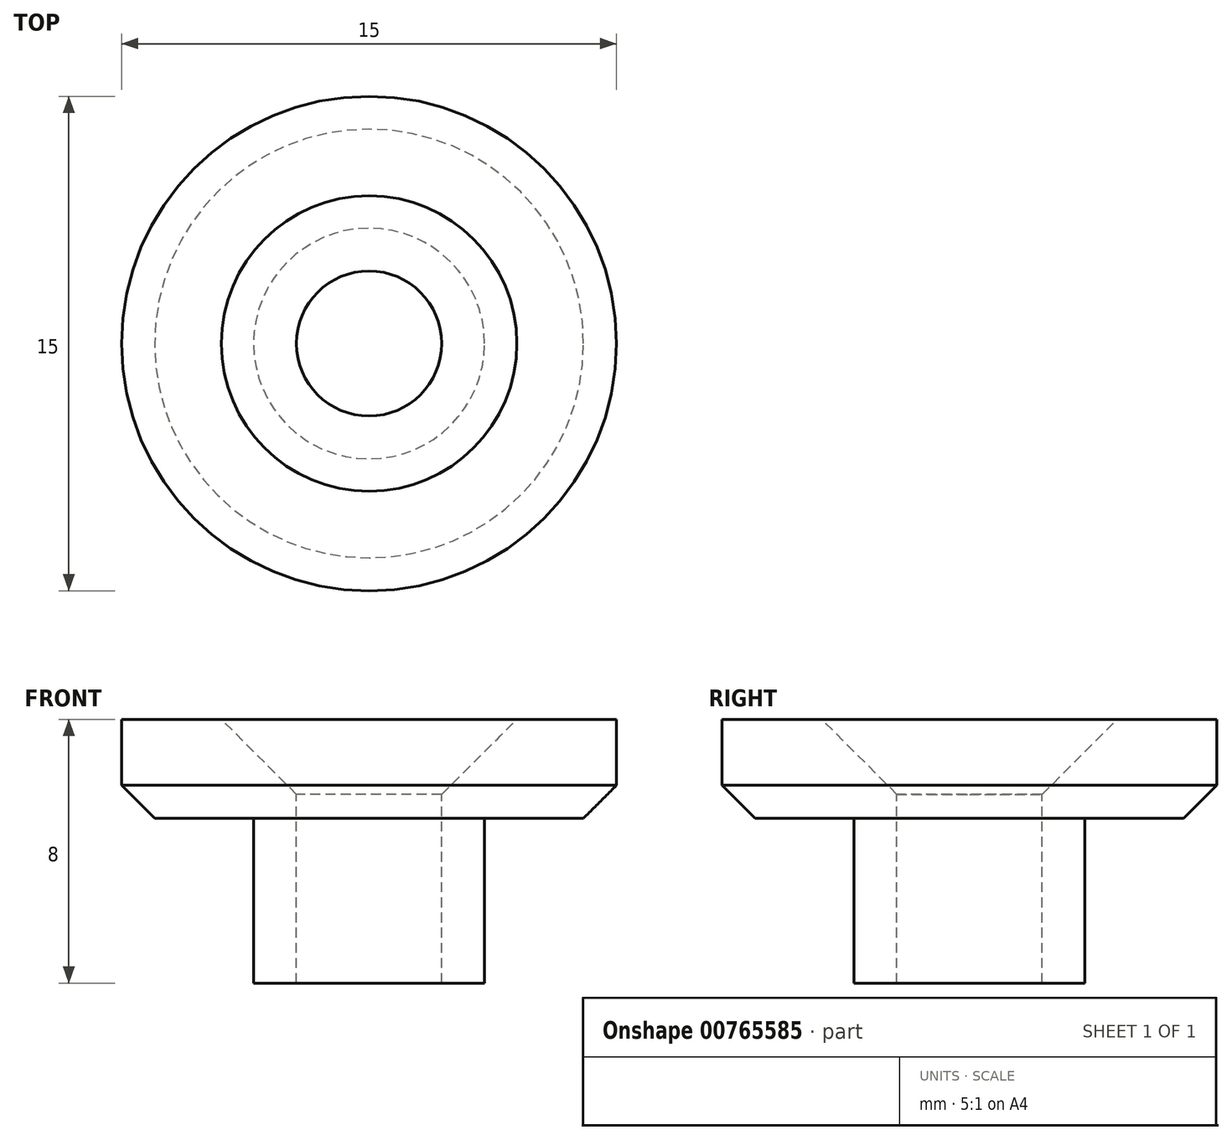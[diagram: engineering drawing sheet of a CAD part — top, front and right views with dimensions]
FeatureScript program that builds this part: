
annotation { "Feature Type Name" : "Feature", "Feature Type Description" : "" }
export const myFeature = defineFeature(function(context is Context, id is Id, definition is map)
    precondition{}
    {
        {
            var Q0;
            Q0=qCreatedBy(makeId("Front.planeOp"),FACE);
            var sketch = newSketch(context, id + "F0", { "sketchPlane" : qUnion([Q0])});
            skLineSegment(sketch, "E0", {"start": v(0, 0) * mm, "end": v(0, 8) * mm});
            skLineSegment(sketch, "E1", {"start": v(0, 8) * mm, "end": v(7.5, 8) * mm});
            skLineSegment(sketch, "E2", {"start": v(7.5, 8) * mm, "end": v(7.5, 5) * mm});
            skLineSegment(sketch, "E3", {"start": v(7.5, 5) * mm, "end": v(3.5, 5) * mm});
            skLineSegment(sketch, "E4", {"start": v(3.5, 5) * mm, "end": v(3.5, 0) * mm});
            skLineSegment(sketch, "E5", {"start": v(3.5, 0) * mm, "end": v(0, 0) * mm});
            skSolve(sketch);
        }
        {
            var Q0;
            Q0=makeQuery(id+"F0.imprint","IMPRINT",FACE,{"disambiguationData":[TD([[makeQuery(id+"F0.imprint","IMPRINT",EDGE,{"derivedFrom":sQuery(id+"F0.wireOp",EDGE,"E0")}),-1.0]])]});
            var Q1;
            Q1=sQuery(id+"F0.wireOp",EDGE,"E0");
            revolve(context, id + "F1", {"surfaceOperationType" : NewSurfaceOperationType.NEW, "entities" : qUnion([Q0]), "axis" : qUnion([Q1]), "revolveType" : RevolveType.FULL});
        }
        {
            var Q0;
            Q0=makeQuery(id+"F1.opRevolve","SWEPT_FACE",FACE,{"disambiguationData":[OSD([sQuery(id+"F0.wireOp",EDGE,"E1")])]});
            var sketch = newSketch(context, id + "F2", { "sketchPlane" : qUnion([Q0])});
            skPoint(sketch, "E6", {"position": v(0, 0) * mm});
            skSolve(sketch);
        }
        {
            var Q0;
            Q0=sQuery(id+"F2.wireOp",VERTEX,"E6");
            var Q1;
            Q1=makeQuery(id+"F1.opRevolve","SWEPT_BODY",BODY,{"disambiguationData":[OSD([sQuery(id+"F0.wireOp",EDGE,"E0"),sQuery(id+"F0.wireOp",EDGE,"E1"),sQuery(id+"F0.wireOp",EDGE,"E2"),sQuery(id+"F0.wireOp",EDGE,"E3"),sQuery(id+"F0.wireOp",EDGE,"E4"),sQuery(id+"F0.wireOp",EDGE,"E5")])]});
            hole(context, id + "F3", {"style" : HoleStyle.C_SINK, "endStyle" : HoleEndStyle.THROUGH, "standardTappedOrClearance" : lookupTablePath({ "standard" : "ISO", "fit" : "Normal", "size" : "M4", "type" : "Clearance" }), "standardBlindInLast" : lookupTablePath({ "fit" : "Standard", "standard" : "ISO", "size" : "M4", "type" : "Clearance" }), "holeDiameter" : 4.4 * mm, "cSinkDiameter" : 8.96 * mm, "cSinkAngle" : 90 * degree, "majorDiameter" : 5 * mm, "isTappedThrough" : true, "tappedDepth" : 12 * mm, "tapClearance" : 3, "locations" : qUnion([Q0]), "scope" : qUnion([Q1])});
        }
        {
            var Q0;
            Q0=makeQuery(id+"F1.opRevolve","SWEPT_EDGE",EDGE,{"disambiguationData":[OSD([sQuery(id+"F0.wireOp",EDGE,"E2"),sQuery(id+"F0.wireOp",EDGE,"E3")])]});
            chamfer(context, id + "F4", {"entities" : qUnion([Q0]), "width" : 1 * mm, "tangentPropagation" : true});
        }
    });
